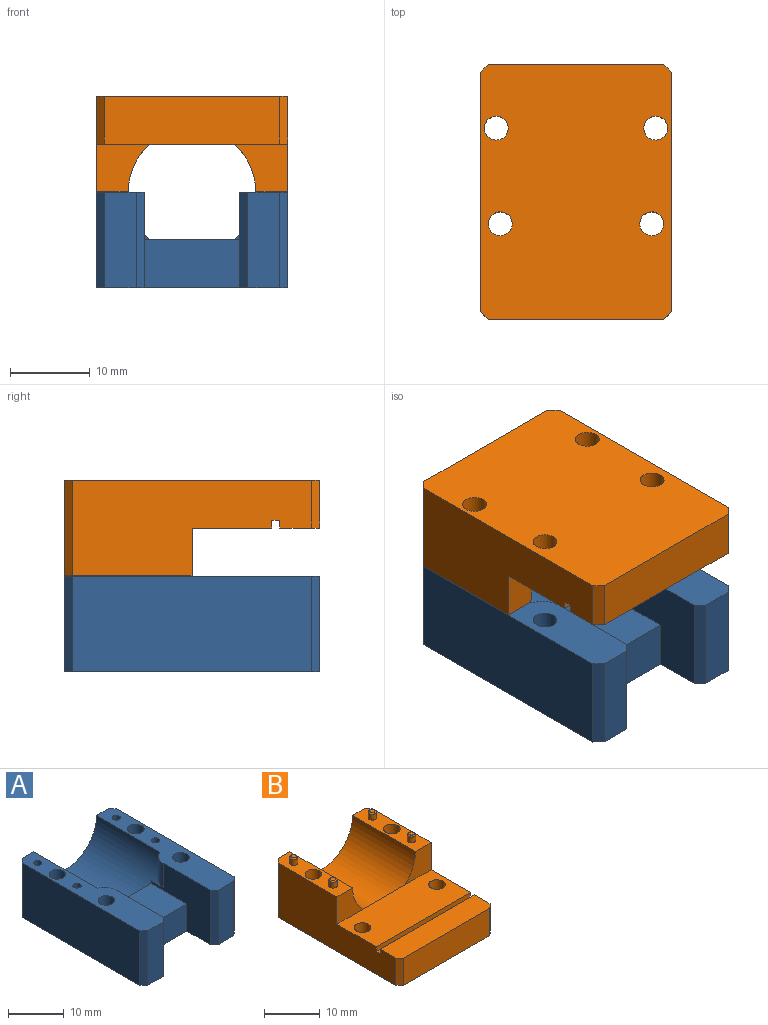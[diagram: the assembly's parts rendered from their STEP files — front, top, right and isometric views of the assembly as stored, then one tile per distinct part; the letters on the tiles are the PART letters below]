
ASSEMBLY  parts=2 mates=1
PART A: 36 faces, bbox 24x32x12 mm
  f0: plane 0.71x0.71mm, normal (0,-1,0), area 0.2mm2, adj f5,f23,f24
  f1: plane 0.62x0.61mm, normal (0,-1,0), area 0.2mm2, adj f5,f23,f27
  f2: plane 32x24mm, normal (0,0,-1), area 652.9mm2, adj f3,f7,f8,f17,f18,f19,f20,f22
  f3: plane 30x12mm, normal (1,0,0), area 360mm2, adj f2,f4,f17,f33
  f4: plane 32x6.07mm, normal (0,0,1), area 139.6mm2, adj f3,f5,f8,f13,f15,f17,f20,f27
  f5: cylinder r=8mm len=19.02mm, axis (0,1,0), area 409.7mm2, adj f0,f1,f4,f6,f8,f21,f24,f27
  f6: plane 32x6mm, normal (0,0,1), area 139mm2, adj f5,f7,f8,f9,f11,f18,f19,f24
  f7: plane 30x12mm, normal (-1,0,0), area 360mm2, adj f2,f6,f18,f32
  f8: plane 22x12mm, normal (0,1,0), area 163.5mm2, adj f2,f4,f5,f6,f17,f18
  f9: cylinder r=0.75mm len=2mm, axis (0,0,1), area 9.4mm2, adj f6,f10
  f10: plane 1.5x1.5mm, normal (0,0,1), area 1.8mm2, adj f9
  f11: cylinder r=0.75mm len=2mm, axis (0,0,1), area 9.4mm2, adj f6,f12
  f12: plane 1.5x1.5mm, normal (0,0,1), area 1.8mm2, adj f11
  f13: cylinder r=0.75mm len=2mm, axis (0,0,1), area 9.4mm2, adj f4,f14
  f14: plane 1.5x1.5mm, normal (0,0,1), area 1.8mm2, adj f13
  f15: cylinder r=0.75mm len=2mm, axis (0,0,1), area 9.4mm2, adj f4,f16
  f16: plane 1.5x1.5mm, normal (0,0,1), area 1.8mm2, adj f15
  f17: plane 12x1mm, normal (0.71,0.71,0), area 17mm2, adj f2,f3,f4,f8
  f18: plane 12x1mm, normal (-0.71,0.71,0), area 17mm2, adj f2,f6,f7,f8
  f19: cylinder r=1.5mm len=12mm, axis (0,0,1), area 113.1mm2, adj f2,f6
  f20: cylinder r=1.5mm len=12mm, axis (0,0,1), area 113.1mm2, adj f2,f4
  f21: plane 10.58x2mm, normal (0,1,0), area 14.5mm2, adj f5,f23
  f22: plane 11.96x6mm, normal (0,-1,0), area 71.8mm2, adj f2,f23,f24,f27
  f23: plane 11.96x9mm, normal (0,0,1), area 107.4mm2, adj f0,f1,f21,f22,f24,f27
  f24: plane 15x12mm, normal (1,0,0), area 110.1mm2, adj f0,f2,f5,f6,f22,f23,f31,f35
  f25: plane 12x4mm, normal (0,-1,0), area 48mm2, adj f2,f6,f31,f32
  f26: cylinder r=1.5mm len=12mm, axis (0,0,-1), area 113.1mm2, adj f2,f6
  f27: plane 15.01x12mm, normal (-1,-0.01,0), area 109.8mm2, adj f1,f2,f4,f5,f22,f23,f30,f34
  f28: plane 12x4.01mm, normal (0,-1,0), area 48.1mm2, adj f2,f4,f30,f33
  f29: cylinder r=1.5mm len=12mm, axis (0,0,-1), area 113.1mm2, adj f2,f4
  f30: plane 12x1mm, normal (-0.71,-0.71,0), area 16.9mm2, adj f2,f4,f27,f28
  f31: plane 12x1mm, normal (0.71,-0.71,0), area 17mm2, adj f2,f6,f24,f25
  f32: plane 12x1mm, normal (-0.71,-0.71,0), area 17mm2, adj f2,f6,f7,f25
  f33: plane 12x1mm, normal (0.71,-0.71,0), area 17mm2, adj f2,f3,f4,f28
  f34: cylinder r=3mm len=5.37mm, axis (0,0,1), area 16mm2, adj f4,f5,f27
  f35: cylinder r=3mm len=5.29mm, axis (0,0,1), area 15.4mm2, adj f5,f6,f24
PART B: 36 faces, bbox 24x32x13.5 mm
  f0: plane 6.71x6mm, normal (0,-1,0), area 29mm2, adj f5,f6,f7,f29
  f1: plane 6.71x6mm, normal (0,-1,0), area 29mm2, adj f3,f4,f5,f29
  f2: plane 32x24mm, normal (0,0,-1), area 737.7mm2, adj f3,f7,f8,f21,f22,f23,f24,f27
  f3: plane 30x12mm, normal (1,0,0), area 269mm2, adj f1,f2,f4,f23,f26,f29,f30,f31
  f4: plane 16x4mm, normal (0,0,1), area 52.9mm2, adj f1,f3,f5,f8,f13,f15,f22,f23
  f5: cylinder r=8mm len=16mm, axis (0,1,0), area 402.1mm2, adj f0,f1,f4,f6,f8,f25
  f6: plane 16x4mm, normal (0,0,1), area 52.9mm2, adj f0,f5,f7,f8,f9,f11,f21,f24
  f7: plane 30x12mm, normal (-1,0,0), area 269mm2, adj f0,f2,f6,f24,f26,f29,f30,f31
  f8: plane 22x12mm, normal (0,1,0), area 163.5mm2, adj f2,f4,f5,f6,f23,f24
  f9: cylinder r=0.75mm len=1.5mm, axis (0,0,-1), area 5.9mm2, adj f6,f20
  f10: plane 1x1mm, normal (0,0,1), area 0.8mm2, adj f20
  f11: cylinder r=0.75mm len=1.5mm, axis (0,0,-1), area 5.9mm2, adj f6,f19
  f12: plane 1x1mm, normal (0,0,1), area 0.8mm2, adj f19
  f13: cylinder r=0.75mm len=1.5mm, axis (0,0,-1), area 5.9mm2, adj f4,f17
  f14: plane 1x1mm, normal (0,0,1), area 0.8mm2, adj f17
  f15: cylinder r=0.75mm len=1.5mm, axis (0,0,-1), area 5.9mm2, adj f4,f18
  f16: plane 1x1mm, normal (0,0,1), area 0.8mm2, adj f18
  f17: cone r=0.75mm half-angle=45deg, axis (0,0,-1), area 1.4mm2, adj f13,f14
  f18: cone r=0.75mm half-angle=45deg, axis (0,0,-1), area 1.4mm2, adj f15,f16
  f19: cone r=0.5mm half-angle=45deg, axis (0,0,-1), area 1.4mm2, adj f11,f12
  f20: cone r=0.5mm half-angle=45deg, axis (0,0,-1), area 1.4mm2, adj f9,f10
  f21: cylinder r=1.5mm len=12mm, axis (0,0,1), area 113.1mm2, adj f2,f6
  f22: cylinder r=1.5mm len=12mm, axis (0,0,1), area 113.1mm2, adj f2,f4
  f23: plane 12x1mm, normal (0.71,0.71,0), area 17mm2, adj f2,f3,f4,f8
  f24: plane 12x1mm, normal (-0.71,0.71,0), area 17mm2, adj f2,f6,f7,f8
  f25: plane 10.58x2mm, normal (0,1,0), area 14.5mm2, adj f5,f29
  f26: plane 24x1mm, normal (0,-1,0), area 24mm2, adj f3,f7,f29,f30
  f27: cylinder r=1.5mm len=6mm, axis (0,0,-1), area 56.5mm2, adj f2,f29
  f28: cylinder r=1.5mm len=6mm, axis (0,0,-1), area 56.5mm2, adj f2,f29
  f29: plane 24x10mm, normal (0,0,1), area 225.9mm2, adj f0,f1,f3,f7,f25,f26,f27,f28
  f30: plane 24x1mm, normal (0,0,1), area 24mm2, adj f3,f7,f26,f31
  f31: plane 24x1mm, normal (0,1,0), area 24mm2, adj f3,f7,f30,f33
  f32: plane 22x6mm, normal (0,-1,0), area 132mm2, adj f2,f33,f34,f35
  f33: plane 24x5mm, normal (0,0,1), area 119mm2, adj f3,f7,f31,f32,f34,f35
  f34: plane 6x1mm, normal (0.71,-0.71,0), area 8.5mm2, adj f2,f3,f32,f33
  f35: plane 6x1mm, normal (-0.71,-0.71,0), area 8.5mm2, adj f2,f7,f32,f33
PLACE A t=(-3.23,-1.62,-6.31)mm
PLACE B rot(axis=(0,1,0),180deg) t=(-3.23,-1.62,-6.28)mm
MATE slider B.f11 <-> A.f13  axis (0,0,1) through (6.77,-14.62,-6.91)mm
